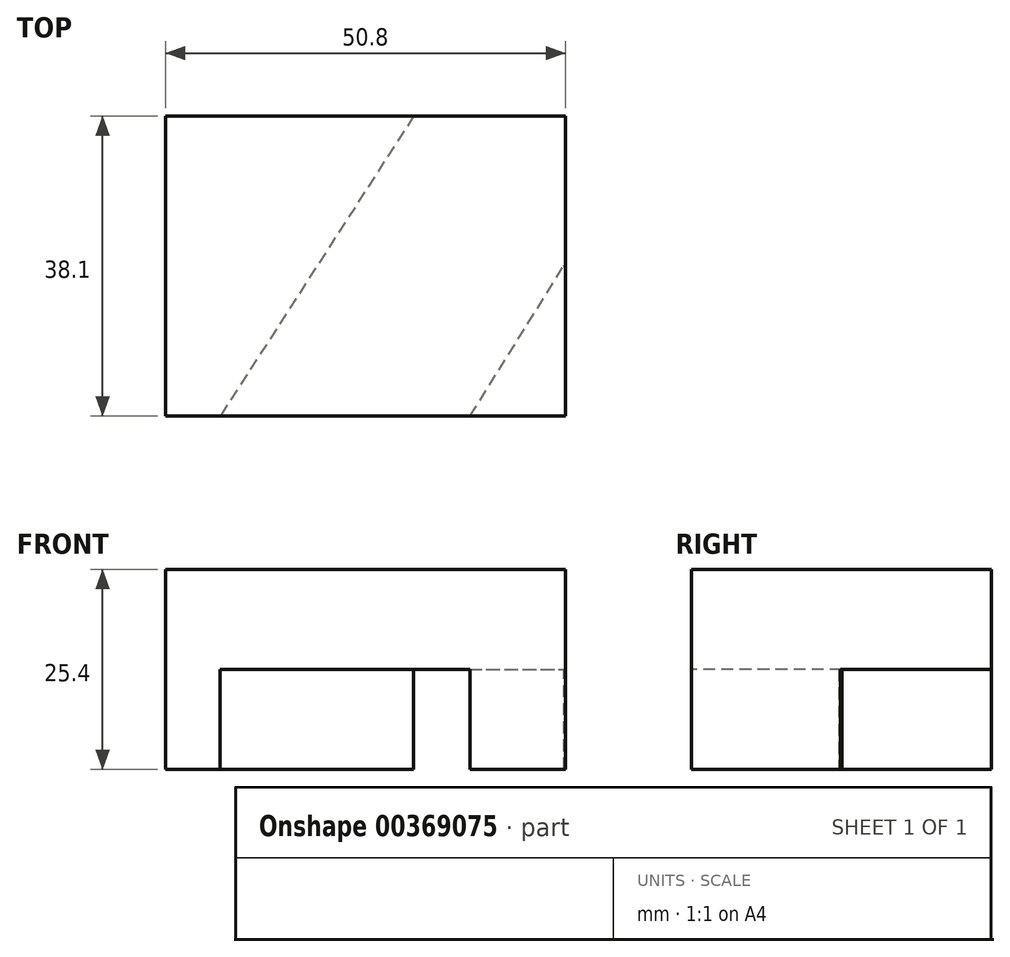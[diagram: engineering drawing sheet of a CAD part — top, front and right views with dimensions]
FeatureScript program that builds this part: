
annotation { "Feature Type Name" : "Feature", "Feature Type Description" : "" }
export const myFeature = defineFeature(function(context is Context, id is Id, definition is map)
    precondition{}
    {
        {
            var Q0;
            Q0=qCreatedBy(makeId("Top.planeOp"),FACE);
            var sketch = newSketch(context, id + "F0", { "sketchPlane" : qUnion([Q0])});
            skLineSegment(sketch, "E0", {"start": v(0, 0) * mm, "end": v(0, 38.1) * mm});
            skLineSegment(sketch, "E1", {"start": v(0, 38.1) * mm, "end": v(50.8, 38.1) * mm});
            skLineSegment(sketch, "E2", {"start": v(50.8, 38.1) * mm, "end": v(50.8, 0) * mm});
            skLineSegment(sketch, "E3", {"start": v(50.8, 0) * mm, "end": v(0, 0) * mm});
            skSolve(sketch);
        }
        {
            var Q0;
            Q0=makeQuery(id+"F0.imprint","IMPRINT",FACE,{"disambiguationData":[TD([[makeQuery(id+"F0.imprint","IMPRINT",EDGE,{"derivedFrom":sQuery(id+"F0.wireOp",EDGE,"E0")}),-1.0]])]});
            extrude(context, id + "F1", {"entities" : qUnion([Q0]), "depth" : 25.4 * mm});
        }
        {
            var Q0;
            Q0=qCreatedBy(makeId("Top.planeOp"),FACE);
            var sketch = newSketch(context, id + "F2", { "sketchPlane" : qUnion([Q0])});
            skLineSegment(sketch, "E4", {"start": v(6.95, 0) * mm, "end": v(38.7, 0) * mm});
            skLineSegment(sketch, "E5", {"start": v(50.67, 38.25) * mm, "end": v(31.62, 38.25) * mm});
            skLineSegment(sketch, "E6", {"start": v(31.62, 38.25) * mm, "end": v(6.95, 0) * mm});
            skLineSegment(sketch, "E7", {"start": v(50.67, 38.25) * mm, "end": v(50.67, 19.2) * mm});
            skLineSegment(sketch, "E8", {"start": v(38.7, 0) * mm, "end": v(50.67, 19.2) * mm});
            skSolve(sketch);
        }
        {
            var Q0;
            Q0 = qSketchRegion(id + "F2", true);
            extrude(context, id + "F3", {"entities" : qUnion([Q0]), "operationType" : NewBodyOperationType.REMOVE, "depth" : 12.7 * mm});
        }
        {
            var Q0;
            Q0=qCreatedBy(makeId("Top.planeOp"),FACE);
            var sketch = newSketch(context, id + "F4", { "sketchPlane" : qUnion([Q0])});
            skLineSegment(sketch, "E9", {"start": v(50.7, 18.74) * mm, "end": v(42.33, 46.3) * mm});
            skLineSegment(sketch, "E10", {"start": v(42.33, 46.3) * mm, "end": v(61.07, 43) * mm});
            skLineSegment(sketch, "E11", {"start": v(61.07, 43) * mm, "end": v(50.7, 18.74) * mm});
            skSolve(sketch);
        }
        {
            var Q0;
            Q0=makeQuery(id+"F4.imprint","IMPRINT",FACE,{"disambiguationData":[TD([[makeQuery(id+"F4.imprint","IMPRINT",EDGE,{"derivedFrom":sQuery(id+"F4.wireOp",EDGE,"E9")}),-1.0]])]});
            extrude(context, id + "F5", {"entities" : qUnion([Q0]), "operationType" : NewBodyOperationType.REMOVE, "depth" : 12.7 * mm});
        }
    });
